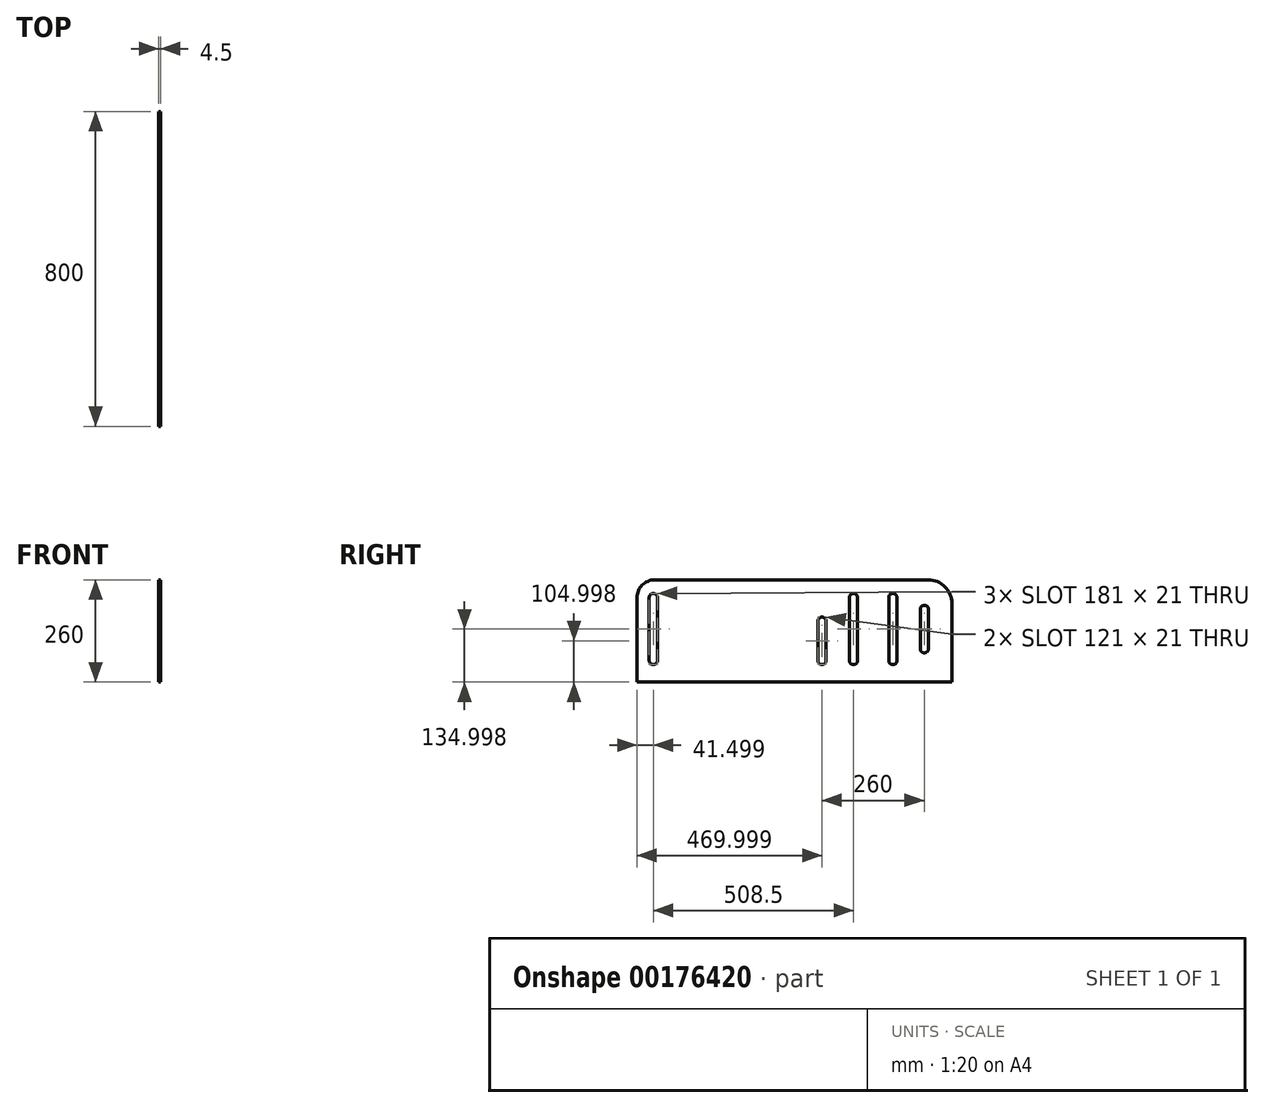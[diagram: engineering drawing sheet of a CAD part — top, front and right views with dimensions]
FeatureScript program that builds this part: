
annotation { "Feature Type Name" : "Feature", "Feature Type Description" : "" }
export const myFeature = defineFeature(function(context is Context, id is Id, definition is map)
    precondition{}
    {
        {
            var Q0;
            Q0=qCreatedBy(makeId("Right.planeOp"),FACE);
            var sketch = newSketch(context, id + "F0", { "sketchPlane" : qUnion([Q0])});
            skLineSegment(sketch, "E0", {"start": v(294.84, -666.4) * mm, "end": v(-100, -666.4) * mm});
            skLineSegment(sketch, "E1", {"start": v(294.84, -666.4) * mm, "end": v(294.84, -466.4) * mm});
            skArc(sketch, "E2", {"start": v(214.34, -581.4) * mm, "mid": v(224.84, -591.9) * mm, "end": v(235.34, -581.4) * mm});
            skLineSegment(sketch, "E3", {"start": v(-105.16, -552.3) * mm, "end": v(294.84, -552.3) * mm, "construction": true});
            skLineSegment(sketch, "E4.trimOffspring", {"start": v(214.34, -481.4) * mm, "end": v(214.34, -581.4) * mm});
            skLineSegment(sketch, "E5.trimOffspring", {"start": v(235.34, -581.4) * mm, "end": v(235.34, -481.4) * mm});
            skLineSegment(sketch, "E6", {"start": v(34.34, -451.4) * mm, "end": v(34.34, -611.4) * mm});
            skArc(sketch, "E7", {"start": v(55.34, -451.4) * mm, "mid": v(44.84, -440.9) * mm, "end": v(34.34, -451.4) * mm});
            skArc(sketch, "E8", {"start": v(34.34, -611.4) * mm, "mid": v(44.84, -621.9) * mm, "end": v(55.34, -611.4) * mm});
            skLineSegment(sketch, "E9.trimOffspring", {"start": v(55.34, -611.4) * mm, "end": v(55.34, -451.4) * mm});
            skArc(sketch, "E10", {"start": v(-45.66, -611.4) * mm, "mid": v(-35.16, -621.9) * mm, "end": v(-24.66, -611.4) * mm});
            skArc(sketch, "E11", {"start": v(-24.66, -511.4) * mm, "mid": v(-35.16, -500.9) * mm, "end": v(-45.66, -511.4) * mm});
            skLineSegment(sketch, "E12.trimOffspring", {"start": v(-45.66, -511.4) * mm, "end": v(-45.66, -611.4) * mm});
            skLineSegment(sketch, "E13.trimOffspring", {"start": v(-24.66, -611.4) * mm, "end": v(-24.66, -511.4) * mm});
            skLineSegment(sketch, "E14", {"start": v(134.34, -451.4) * mm, "end": v(134.34, -611.4) * mm});
            skArc(sketch, "E15", {"start": v(155.34, -451.4) * mm, "mid": v(144.84, -440.9) * mm, "end": v(134.34, -451.4) * mm});
            skArc(sketch, "E16", {"start": v(134.34, -611.4) * mm, "mid": v(144.84, -621.9) * mm, "end": v(155.34, -611.4) * mm});
            skLineSegment(sketch, "E17.trimOffspring", {"start": v(155.34, -611.4) * mm, "end": v(155.34, -451.4) * mm});
            skArc(sketch, "E18", {"start": v(235.34, -481.4) * mm, "mid": v(224.84, -470.9) * mm, "end": v(214.34, -481.4) * mm});
            skPoint(sketch, "E19.end.orphan", {"position": v(0, 0) * mm});
            skLineSegment(sketch, "E20", {"start": v(-100, -611.4) * mm, "end": v(294.84, -611.4) * mm, "construction": true});
            skLineSegment(sketch, "E21", {"start": v(26.93, -451.4) * mm, "end": v(235.44, -451.4) * mm, "construction": true});
            skArc(sketch, "E22", {"start": v(-474.16, -611.4) * mm, "mid": v(-463.66, -621.9) * mm, "end": v(-453.16, -611.4) * mm});
            skLineSegment(sketch, "E23", {"start": v(-505.16, -451.4) * mm, "end": v(-505.16, -666.4) * mm});
            skArc(sketch, "E24", {"start": v(-453.16, -451.4) * mm, "mid": v(-463.66, -440.9) * mm, "end": v(-474.16, -451.4) * mm});
            skPoint(sketch, "E25.orphan", {"position": v(-505.16, -455) * mm});
            skPoint(sketch, "E26.visualSharp", {"position": v(-417, -611.4) * mm});
            skLineSegment(sketch, "E27", {"start": v(-100, -666.4) * mm, "end": v(-505.16, -666.4) * mm});
            skLineSegment(sketch, "E28", {"start": v(-453.16, -451.4) * mm, "end": v(-453.16, -611.4) * mm});
            skLineSegment(sketch, "E29", {"start": v(-474.16, -611.4) * mm, "end": v(-474.16, -451.4) * mm});
            skLineSegment(sketch, "E30", {"start": v(234.84, -406.4) * mm, "end": v(-460.16, -406.4) * mm});
            skPoint(sketch, "E31.start.orphan", {"position": v(-422.3, -451.4) * mm});
            skArc(sketch, "E32.filletArc", {"start": v(-460.16, -406.4) * mm, "mid": v(-491.98, -419.58) * mm, "end": v(-505.16, -451.4) * mm});
            skPoint(sketch, "E33.visualSharp", {"position": v(294.84, -406.4) * mm});
            skArc(sketch, "E33.filletArc", {"start": v(294.84, -466.4) * mm, "mid": v(277.27, -423.98) * mm, "end": v(234.84, -406.4) * mm});
            skSolve(sketch);
        }
        {
            var Q0;
            Q0=makeQuery(id+"F0.imprint","IMPRINT",FACE,{"disambiguationData":[TD([[makeQuery(id+"F0.imprint","IMPRINT",EDGE,{"derivedFrom":sQuery(id+"F0.wireOp",EDGE,"E0")}),-1.0]])]});
            var Q1;
            Q1=makeQuery(id+"F0.imprint","IMPRINT",FACE,{"disambiguationData":[TD([[makeQuery(id+"F0.imprint","IMPRINT",EDGE,{"derivedFrom":sQuery(id+"F0.wireOp",EDGE,"796f1464-cd0d-4846-830b-1ebac3a17c7c")}),-1.0]])]});
            extrude(context, id + "F1", {"entities" : qUnion([Q0, Q1]), "depth" : 4.5 * mm});
        }
    });
